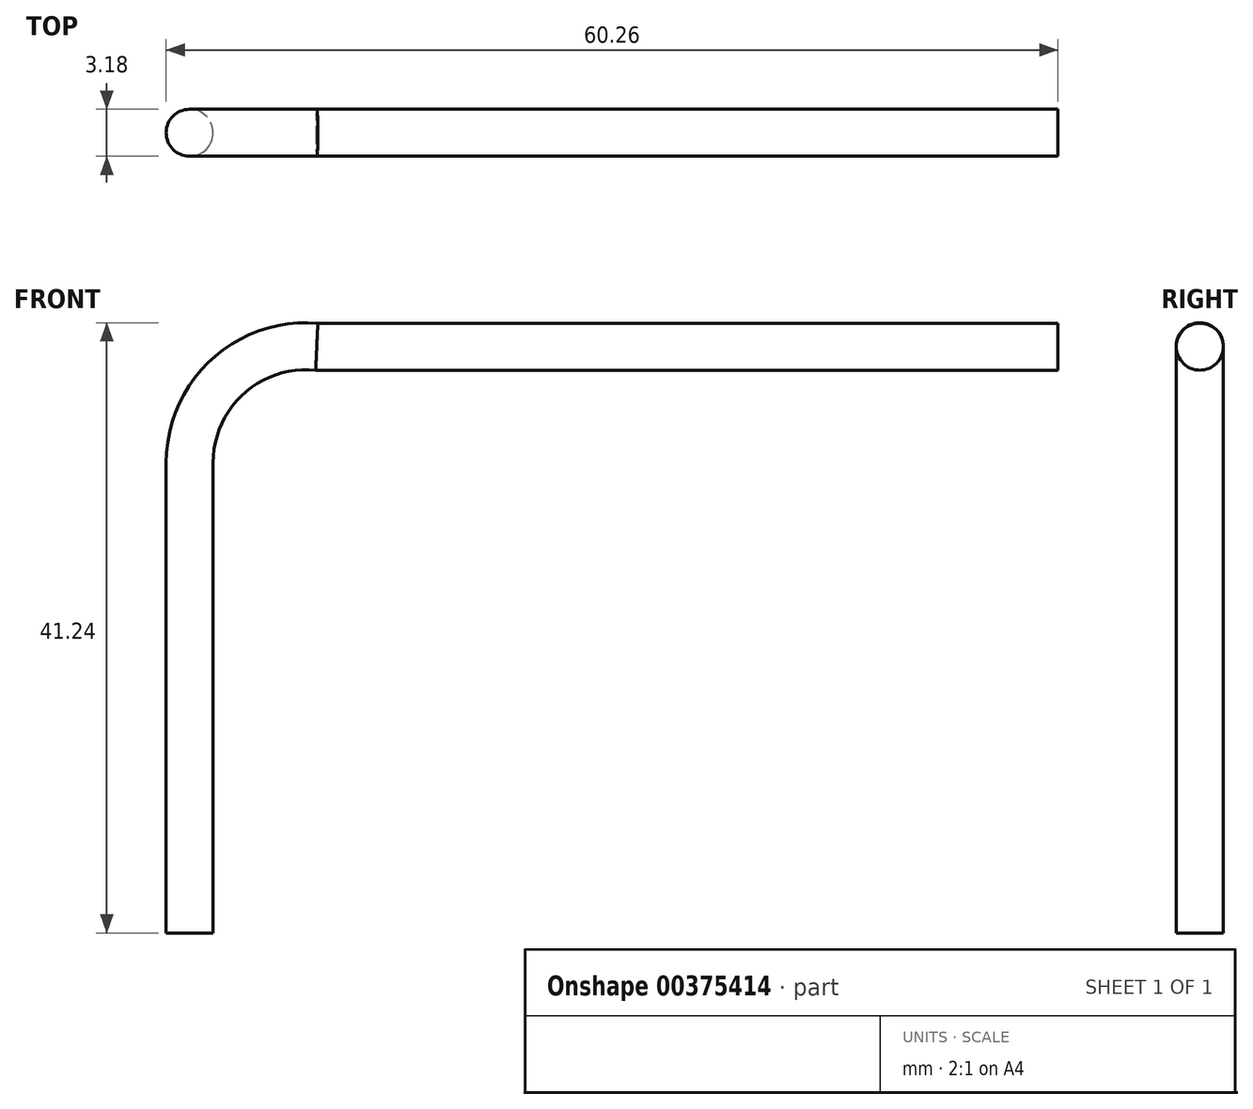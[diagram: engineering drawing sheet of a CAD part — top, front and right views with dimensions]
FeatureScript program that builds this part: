
annotation { "Feature Type Name" : "Feature", "Feature Type Description" : "" }
export const myFeature = defineFeature(function(context is Context, id is Id, definition is map)
    precondition{}
    {
        {
            var Q0;
            Q0=qCreatedBy(makeId("Top.planeOp"),FACE);
            var sketch = newSketch(context, id + "F0", { "sketchPlane" : qUnion([Q0])});
            skCircle(sketch, "E0", {"center": v(0, 0) * mm, "radius": 1.59 * mm});
            skSolve(sketch);
        }
        {
            var Q0;
            Q0=qCreatedBy(makeId("Front.planeOp"),FACE);
            var sketch = newSketch(context, id + "F1", { "sketchPlane" : qUnion([Q0])});
            skLineSegment(sketch, "E1", {"start": v(0, 0) * mm, "end": v(0, 31.78) * mm});
            skArc(sketch, "E2", {"start": v(8.6, 39.62) * mm, "mid": v(2.57, 37.6) * mm, "end": v(0, 31.78) * mm});
            skLineSegment(sketch, "E3", {"start": v(8.6, 39.62) * mm, "end": v(58.67, 39.62) * mm});
            skSolve(sketch);
        }
        {
            var Q0;
            Q0=qSketchRegion(id+"F0",true);
            var Q1;
            Q1=qConstructionFilter(qBodyType(qCreatedBy(id+"F1",EDGE),BodyType.WIRE),ConstructionObject.NO);
            sweep(context, id + "F2", {"profiles" : qUnion([Q0]), "path" : qUnion([Q1])});
        }
    });
